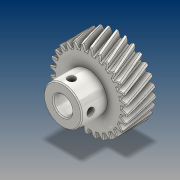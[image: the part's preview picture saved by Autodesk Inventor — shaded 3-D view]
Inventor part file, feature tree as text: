
AUTODESK INVENTOR PART (.ipt)
format: ipt  version: 2021 (Build 250183000, 183)  size: 971,776 bytes
history: native  units: mm (DEFAULTED — no unit token found)
features: sketch x6, extrude x5, plane x4, other x4, chamfer x2, pattern_circular x1, loft x1, projected_geometry x1
ambient origin geometry x8: Origin, YZ Plane, XZ Plane, XY Plane, X Axis, Y Axis, Z Axis, Center Point
bodies: Solid1 (feature_tree)
feature tree (24):
  extrude  "Extrusion1"  Depth=15.0mm TaperAngle=0.0deg
  plane  "Work Plane2"
  plane  "Work Plane8"
  plane  "Work Plane9"
  other  "Spur Gear"
  sketch  "Sketch3"  dims[d16=45.0mm d17=0.0mm d34=1.121997mm]
  extrude  "Extrusion2"  Depth=10.0mm TaperAngle=0.0deg
  extrude  "Extrusion3"  Depth=1.121997mm TaperAngle=0.0deg
  chamfer  "Chamfer1"  Distance=45.0mm
  chamfer  "Chamfer2"  [1 undecoded]
  extrude  "Extrusion4"  Depth=9.6mm
  pattern_circular  "Circular Pattern1"  [2 undecoded]
  plane  "Work Plane11"
  loft  "Loft1"
  extrude  "Extrusion5"  Depth=13.0mm TaperAngle=0.0deg
  sketch  "Sketch1"  dims[d0=39.395974mm d1=15.0mm d2=0.0mm]
  sketch  "Sketch2"  dims[d3=37.246222mm d4=10.0mm d5=0.0mm]
  other  "Srf1"
  sketch  "Sketch4"  dims[d39=0.0mm]
  projected_geometry  "Projected Loop1"
  sketch  "Sketch5"  dims[d41=0.0mm]
  other  "Edges1"
  sketch  "Sketch6"  dims[d43=45.0mm d46=45.0mm d47=0.0mm d48=0.0mm d49=9.6mm d50=5.0mm d51=69.5mm d52=0.0mm d53=13.0mm d54=0.0mm d55=0.5mm d56=2.0mm d57=45.0deg d58=0.5mm d59=2.0mm d60=45.0deg d62=4.0mm d63=3.8mm d64=10.0mm d65=0.0mm d66=20.0mm d67=90.0deg d69=4.0mm d70=0.0mm d71=90.0deg d72=0.0mm d73=90.0deg d74=46.25mm d75=0.0mm]
  other  "Pitch Diameter"
note: 3 required parameter values undecoded (feature->parameter linkage not recoverable at this tier; creation-order binding heuristic only, values carry confidence <= 0.55)
